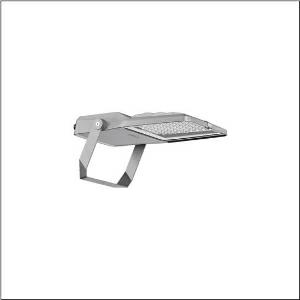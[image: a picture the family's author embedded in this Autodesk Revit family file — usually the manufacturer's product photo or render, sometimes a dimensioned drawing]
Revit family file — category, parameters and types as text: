
# Revit family: floodlight_fl_21_iq_mini___pl52_5xa7772b3d1a_2253
name_source: partatom
category: Lighting Fixtures
units: mm (PartAtom-declared; Revit-internal decimal feet)

## family parameters
Cut with Voids When Loaded = No
Host = Face
Light Source = No
Part Type = Normal
Room Calculation Point = No
Round Connector Dimension = Use Diameter
Shared = No

## types (1)
- --- (1 x LED, 5370 lm, 45.5 W, 3000K)
    Apparent Load = 46 VA
    CIE Flux Codes = 26 60 98 100 100
    Color Rendering = 80
    Color Temperature = 3000K
    Default Elevation = 1800 mm
    Description = Floodlight FL 21 iQ mini, floodlight, primary light control with lens, of PMMA, primary optical cover: protective disc, of toughened safety glass, transparent, light distribution: PL52, light emission: direct distribution, installation type: surface-mounted, lamps: LED, High Power LED, rated values: 5.370lm | 45,5W | 118lm/W (begin service life); end service life: 5.370lm | 48W; at 50% lumin. flux: 2.685lm | 21,4W | 125,5lm/W, colour temperature: 3000K, colour rendering: CRI > 80, light colour: 830, light setting 1 begin service life: 100% | 5.370lm | 45,5W | 118lm/W | 3.000K, light setting 1 end service life: 48W, further light settings possible, control: Street-Remote, Auto-Match, Temp-Guard, Night-Set, Smart-Wire, Desk-Remote (wireless, voltage-free reading and setting of iQ features in the workshop via application-optimized NFC function/RFID function), optimised constant luminous flux control (CLO 2.0), pre-setting: linear dimming characteristic, with terminal, 6-pole, mains connection: 220..240V, AC, 50/60Hz, luminaire housing, of diecast aluminium, powder-coated, SITECO metallic grey (DB 702S), corrosivity category C5 mid according to DIN EN ISO 12944suitable for swimming poolschlorine-resistant, sealing non-destructively replaceable, mounting bracket, of steel, galvanised, powder-coated, SITECO metallic grey (DB 702S), protection rating (complete): IP66, insulation class (complete): insulation class II (safety insulation), certification: CE, ENEC, VDE, protection symbol: D, impact resistance: IK08, permissible operating ambient temperature: -40..+40°C, permissible operating ambient temperature for outdoor applications: -40..+50°C, standard: DIN EN 12944, LABS conformity tested according to VDMA 24364:2018-05, packaging unit: 1 piece

Light Distribution: PL52
    Height = 70 mm
    Lamp = 1 x LED
    Lamp Light Flux = 5370 lm
    Lamp Power = 45.5 W
    Lamp count = 1
    Length = 485 mm
    Luminous efficacy = 118 lm/W
    Manufacturer = Siteco
    ModVariant = No
    Model = 5XA7772B3D1A
    Number of Poles = 1
    OnlyDefault = Yes
    Power Factor = 1
    Product Name = Floodlight FL 21 iQ mini | PL52
    Product group = floodlight | pylon annexe
    ProductGroupID = 6201
    Protection Class = Protection class II
    Protection Degree = IP 66
    RLX_Detail_Level = 1
    RLX_Emergency_Light_Flux = 0 lm
    RLX_Emergency_Type = 0
    RLX_Emergency_Type_DB = No
    RlxData = <blob elided: 96701 chars, md5=9f3ccd29>
    Socket = socket
    Standby Power = 0 W
    System Light Flux = 5370 lm
    System Power = 46 W
    Type Comments = factory setting: luminous flux: 100 % | dim-lin: 254 | 463 mA
    Type Image = l_1006845.jpg
    URL = http://relux.com
    VarID = @adj_164277
    Voltage = 0 V
    Weight = 0.00 kg
    Width = 337 mm

## geometry (parser evidence)
native form markers: Blend x4, Sweep x13
no freeform markers — native parametric forms only
